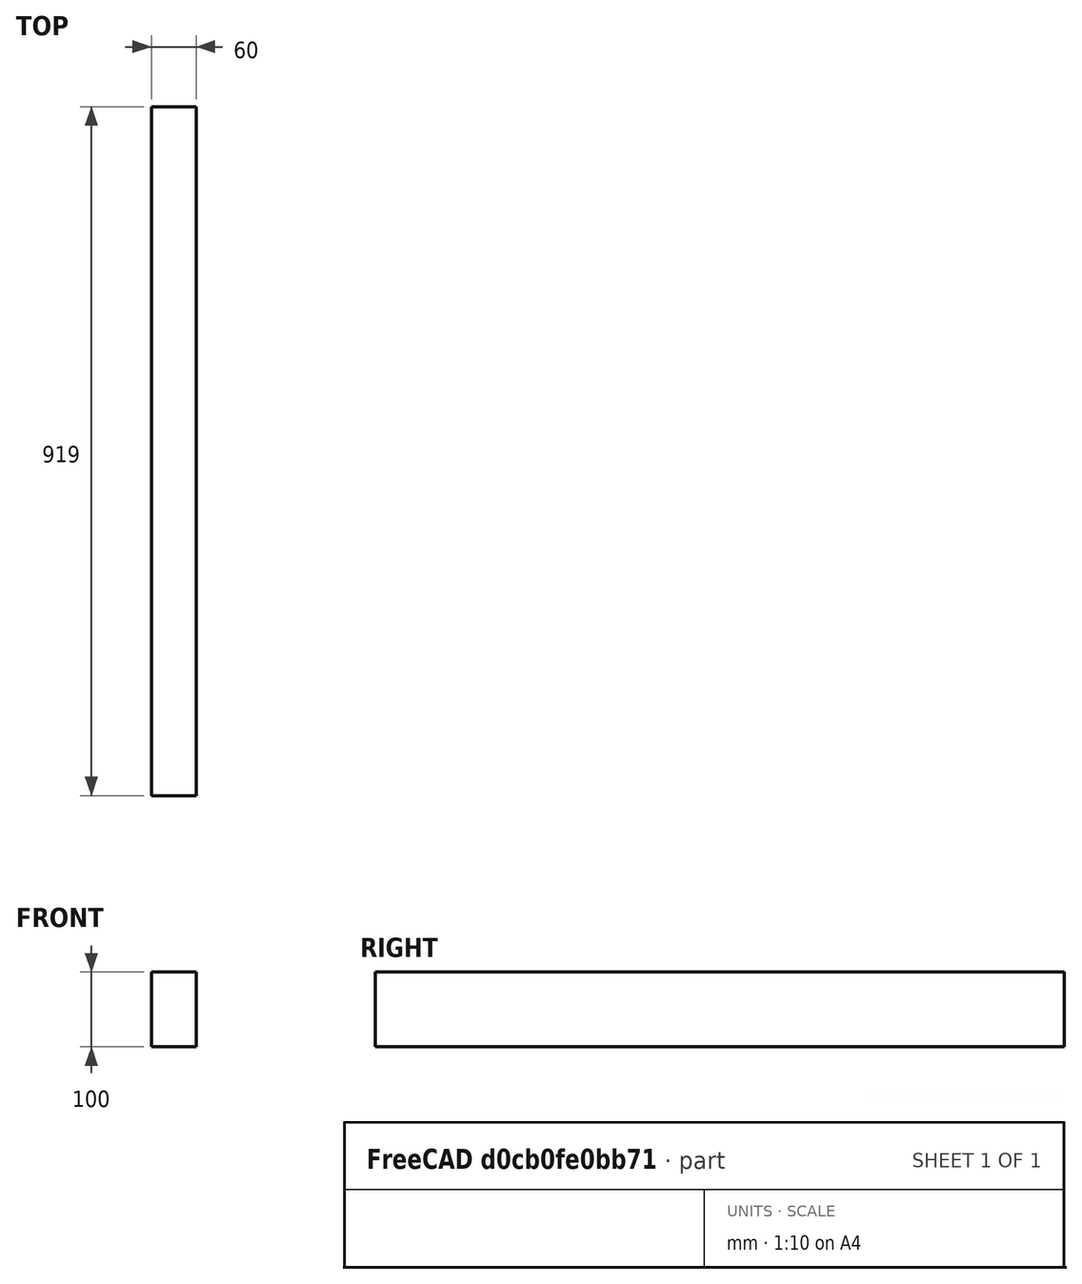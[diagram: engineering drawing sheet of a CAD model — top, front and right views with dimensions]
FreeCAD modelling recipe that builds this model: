
FCSTD DOCUMENT  (FreeCAD 1.0RUnknown)
Label: beam60x100x919
License: All rights reserved
LicenseURL: https://en.wikipedia.org/wiki/All_rights_reserved
objects: PartDesign::CoordinateSystem×3, Sketcher::SketchObject×1, PartDesign::Pad×1, PartDesign::Body×1, App::Part×1
note: 9 computed .brp shape members not serialized (recipe doc carries the construction recipe); baked Part::Feature solids carry a one-line shape summary decoded from their .brp

FEATURE [Sketcher::SketchObject] Sketch
  ArcFitTolerance = 1e-06
  AttachmentSupport = -> [XZ_Plane]
  FullyConstrained = true
  MakeInternals = false
  MapMode = 5
  Placement = pos=(0,0,0) rot=(1,0,0;1.5708rad)
  sketch-geometry (5):
    g0: LineSegment StartX=-30 StartY=-50 StartZ=0 EndX=30 EndY=-50 EndZ=0
    g1: LineSegment StartX=30 StartY=-50 StartZ=0 EndX=30 EndY=50 EndZ=0
    g2: LineSegment StartX=30 StartY=50 StartZ=0 EndX=-30 EndY=50 EndZ=0
    g3: LineSegment StartX=-30 StartY=50 StartZ=0 EndX=-30 EndY=-50 EndZ=0
    g4: GeomPoint [constr] X=0 Y=0 Z=0
  constraints (12):
    c: Coincident(g0,g1)
    c: Coincident(g1,g2)
    c: Coincident(g2,g3)
    c: Coincident(g3,g0)
    c: Horizontal(g0)
    c: Horizontal(g2)
    c: Vertical(g1)
    c: Vertical(g3)
    c: Symmetric(g2,g0,g4)
    c: Coincident(g4,g-1)
    c: DistanceX(g0,g0) = 60
    c: DistanceY(g3,g3) = 100
FEATURE [PartDesign::Pad] Pad
  Direction = (0,-1,2e-16)
  Length = 919
  Length2 = 10
  Midplane = true
  Placement = pos=(0,0,0) rot=(1,0,0;1.5708rad)
  Profile = -> Sketch
  ReferenceAxis = -> Sketch [N_Axis]
  Refine = true
  Suppressed = false
  Type = 0
FEATURE [PartDesign::Body] Body  label="Körper"
  AllowCompound = false
  Group = -> [Sketch,Pad]
  Origin = -> Origin
  Tip = -> Pad
FEATURE [PartDesign::CoordinateSystem] LCS_Origin
  AttacherType = Attacher::AttachEngine3D
  AttachmentSupport = -> [X_Axis001]
  MapMode = 2
FEATURE [PartDesign::CoordinateSystem] LCS_1
  AttacherType = Attacher::AttachEngine3D
  AttachmentSupport = -> [Pad]
  MapMode = 45
  Placement = pos=(-30,459.5,-2.04e-13) rot=(0,0,1;0rad)
FEATURE [PartDesign::CoordinateSystem] LCS_2
  AttacherType = Attacher::AttachEngine3D
  AttachmentSupport = -> [Pad]
  MapMode = 45
  Placement = pos=(-30,-459.5,2.04e-13) rot=(0,0,1;0rad)
FEATURE [App::Part] beam60x100x887  label="beam60x100x1100"
  Group = -> [LCS_Origin,Body,LCS_1,LCS_2]
  Origin = -> Origin001
